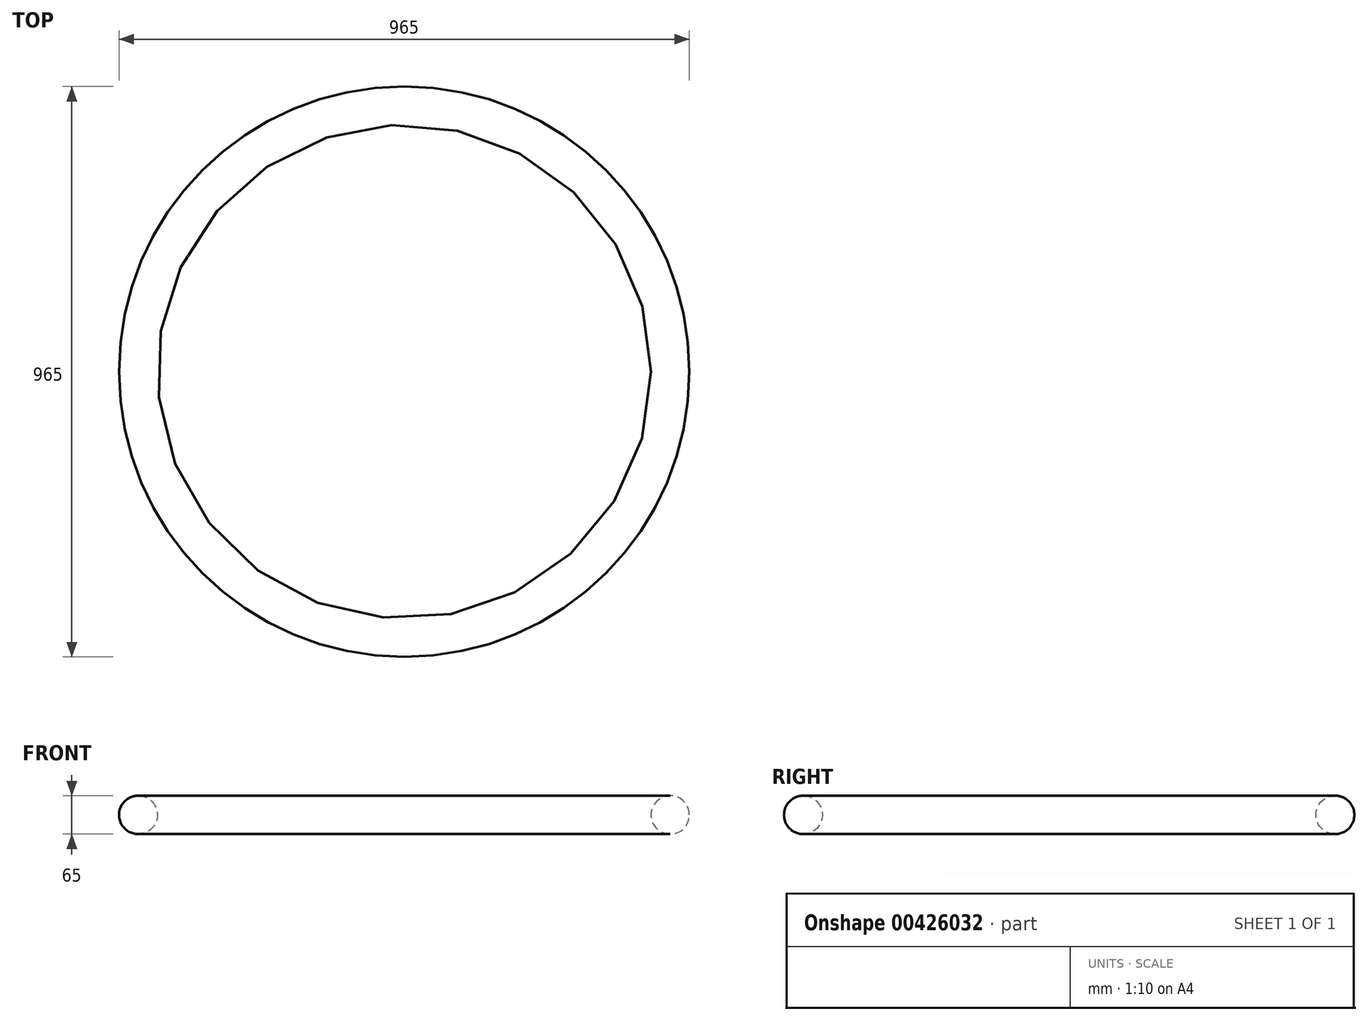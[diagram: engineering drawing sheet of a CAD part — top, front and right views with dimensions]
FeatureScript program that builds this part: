
annotation { "Feature Type Name" : "Feature", "Feature Type Description" : "" }
export const myFeature = defineFeature(function(context is Context, id is Id, definition is map)
    precondition{}
    {
        {
            var Q0;
            Q0=qCreatedBy(makeId("Front.planeOp"),FACE);
            var sketch = newSketch(context, id + "F0", { "sketchPlane" : qUnion([Q0])});
            skCircle(sketch, "E0", {"center": v(-450, 0) * mm, "radius": 32.5 * mm});
            skLineSegment(sketch, "E1", {"start": v(0, 82.13) * mm, "end": v(0, -115.9) * mm, "construction": true});
            skSolve(sketch);
        }
        {
            var Q0;
            Q0=makeQuery(id+"F0.imprint","IMPRINT",FACE,{"disambiguationData":[TD([[makeQuery(id+"F0.imprint","IMPRINT",EDGE,{"derivedFrom":sQuery(id+"F0.wireOp",EDGE,"E0")}),1.0]])]});
            var Q1;
            Q1=sQuery(id+"F0.wireOp",EDGE,"E1");
            revolve(context, id + "F1", {"surfaceOperationType" : NewSurfaceOperationType.NEW, "entities" : qUnion([Q0]), "axis" : qUnion([Q1]), "revolveType" : RevolveType.FULL});
        }
    });
